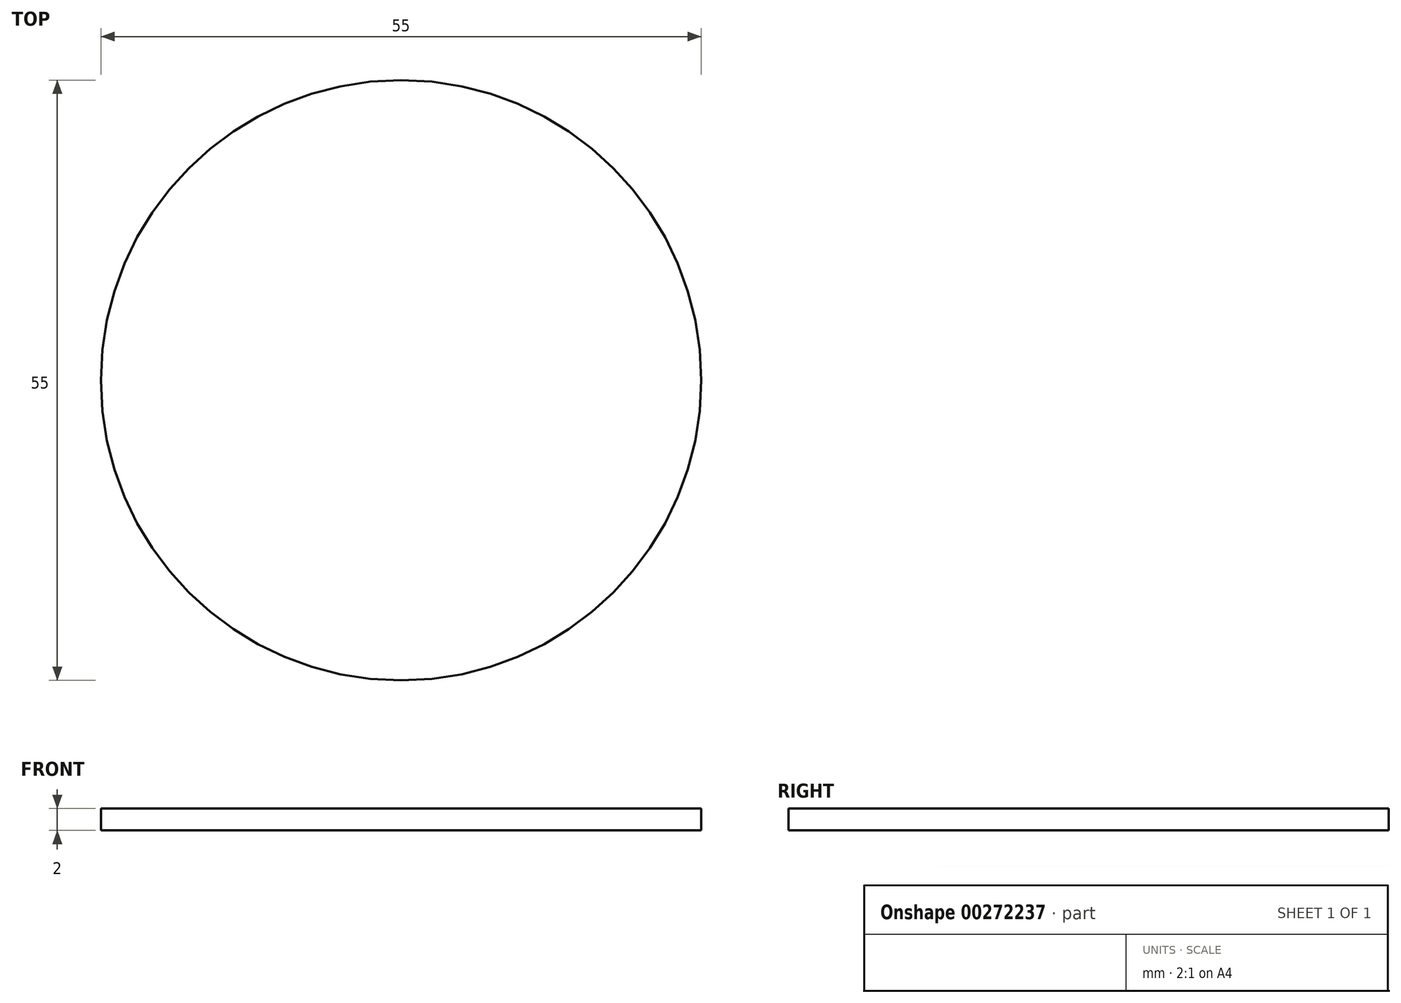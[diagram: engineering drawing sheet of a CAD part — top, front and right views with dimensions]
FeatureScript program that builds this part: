
annotation { "Feature Type Name" : "Feature", "Feature Type Description" : "" }
export const myFeature = defineFeature(function(context is Context, id is Id, definition is map)
    precondition{}
    {
        {
            var Q0;
            Q0=qCreatedBy(makeId("Top.planeOp"),FACE);
            var sketch = newSketch(context, id + "F0", { "sketchPlane" : qUnion([Q0])});
            skCircle(sketch, "E0", {"center": v(0, 0) * mm, "radius": 27.5 * mm});
            skSolve(sketch);
        }
        {
            var Q0;
            Q0=makeQuery(id+"F0.imprint","IMPRINT",FACE,{"disambiguationData":[TD([[makeQuery(id+"F0.imprint","IMPRINT",EDGE,{"derivedFrom":sQuery(id+"F0.wireOp",EDGE,"E0")}),1.0]])]});
            extrude(context, id + "F1", {"entities" : qUnion([Q0]), "depth" : 2 * mm});
        }
    });
